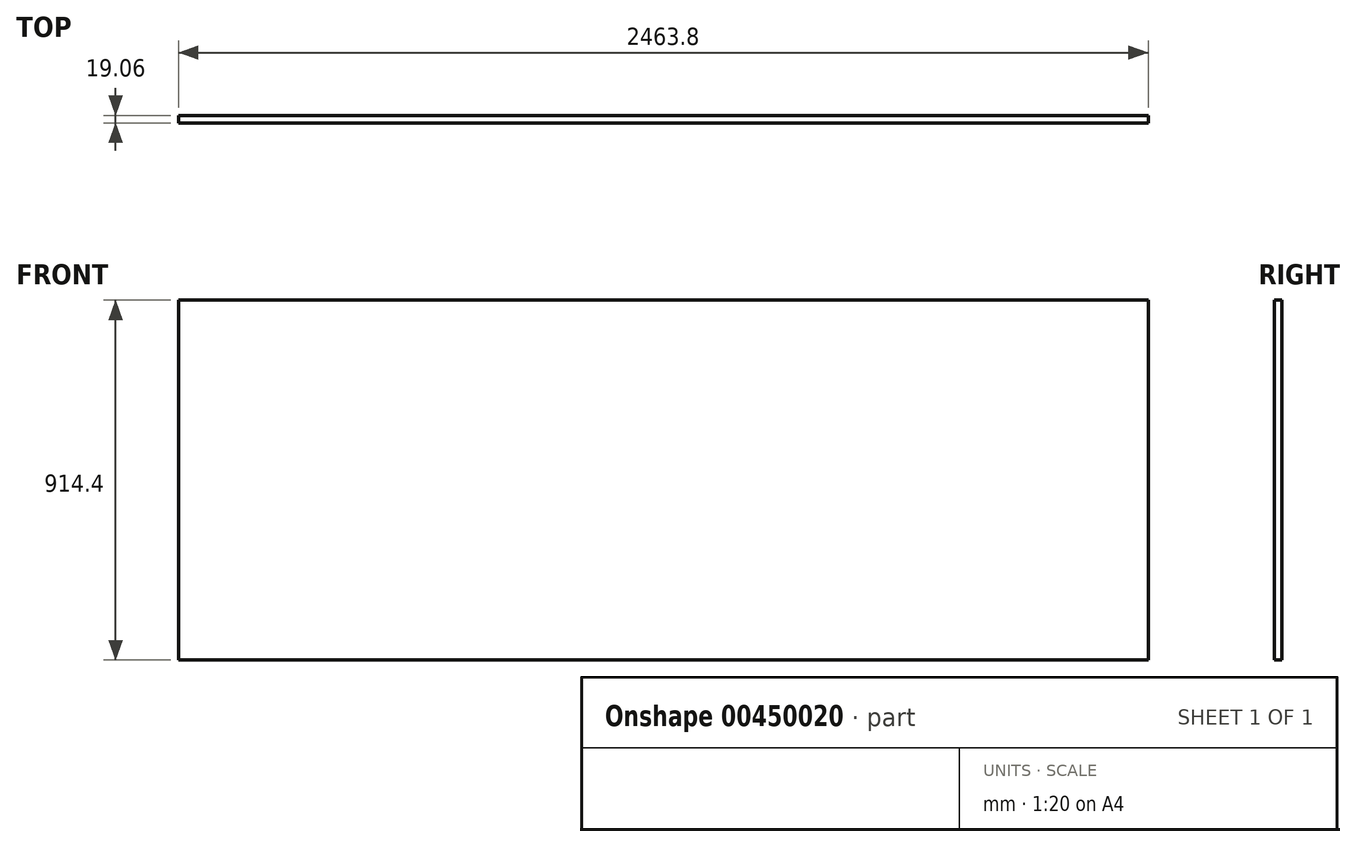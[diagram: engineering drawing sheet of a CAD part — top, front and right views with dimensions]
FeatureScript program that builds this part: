
annotation { "Feature Type Name" : "Feature", "Feature Type Description" : "" }
export const myFeature = defineFeature(function(context is Context, id is Id, definition is map)
    precondition{}
    {
        {
            var Q0;
            Q0=qCreatedBy(makeId("Front.planeOp"),FACE);
            var sketch = newSketch(context, id + "F0", { "sketchPlane" : qUnion([Q0])});
            skLineSegment(sketch, "E0", {"start": v(0, 0) * mm, "end": v(0, 54.54) * mm, "construction": true});
            skLineSegment(sketch, "E1", {"start": v(0, 0) * mm, "end": v(2463.8, 0) * mm, "construction": true});
            skLineSegment(sketch, "E2.bottom", {"start": v(0, 457.2) * mm, "end": v(2463.8, 457.2) * mm});
            skLineSegment(sketch, "E2.top", {"start": v(0, -457.2) * mm, "end": v(2463.8, -457.2) * mm});
            skLineSegment(sketch, "E2.left", {"start": v(0, 457.2) * mm, "end": v(0, -457.2) * mm});
            skLineSegment(sketch, "E2.right", {"start": v(2463.8, 457.2) * mm, "end": v(2463.8, -457.2) * mm});
            skSolve(sketch);
        }
        {
            var Q0;
            Q0=makeQuery(id+"F0.imprint","IMPRINT",FACE,{"disambiguationData":[TD([[makeQuery(id+"F0.imprint","IMPRINT",EDGE,{"derivedFrom":sQuery(id+"F0.wireOp",EDGE,"E2.bottom")}),-1.0]])]});
            extrude(context, id + "F1", {"entities" : qUnion([Q0]), "endBound" : BoundingType.SYMMETRIC, "depth" : 19.05 * mm});
        }
    });
